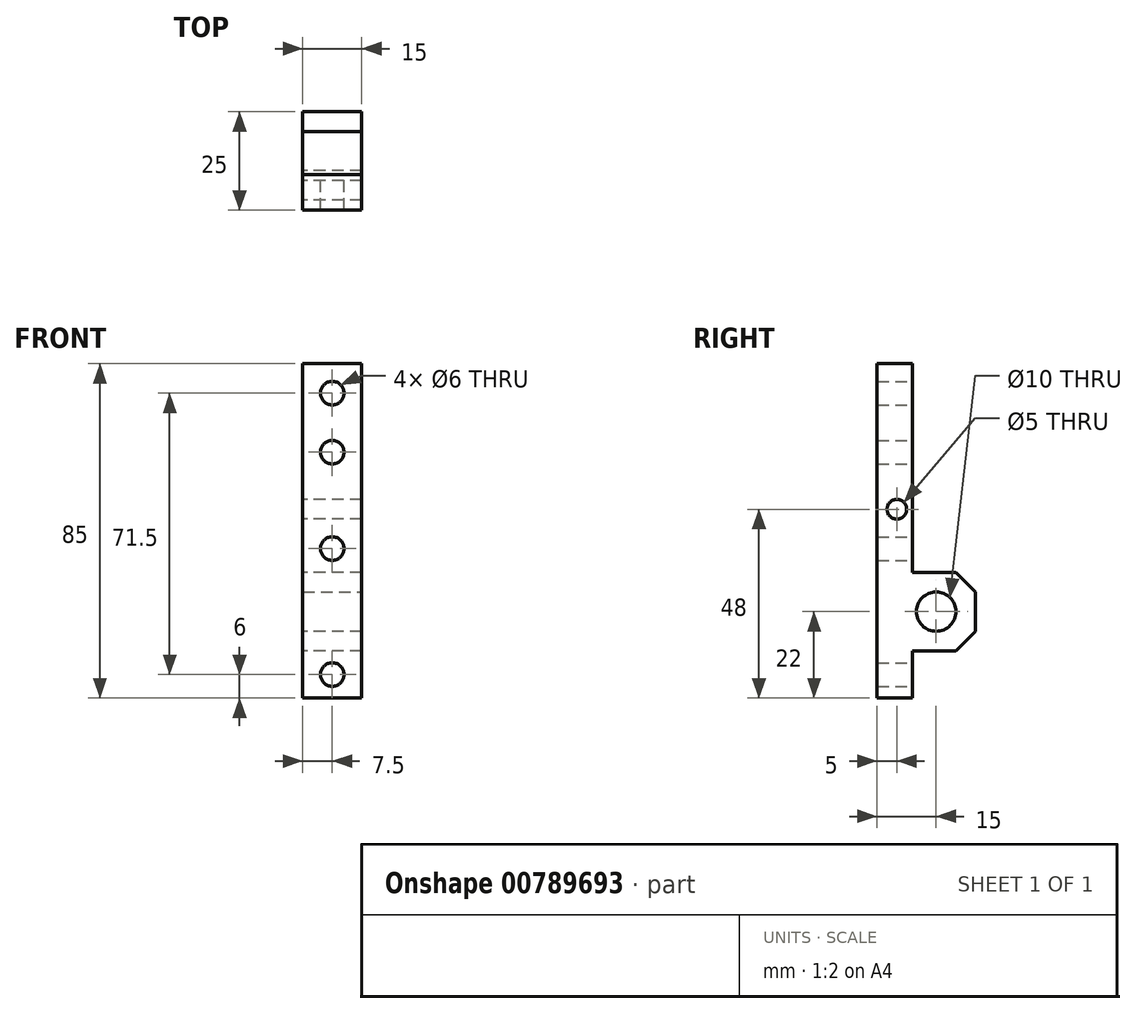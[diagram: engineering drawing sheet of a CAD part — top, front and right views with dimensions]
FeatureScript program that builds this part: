
annotation { "Feature Type Name" : "Feature", "Feature Type Description" : "" }
export const myFeature = defineFeature(function(context is Context, id is Id, definition is map)
    precondition{}
    {
        {
            var Q0;
            Q0=qCreatedBy(makeId("Right.planeOp"),FACE);
            var sketch = newSketch(context, id + "F0", { "sketchPlane" : qUnion([Q0])});
            skLineSegment(sketch, "E0", {"start": v(0, 0) * mm, "end": v(0, 85) * mm});
            skLineSegment(sketch, "E1", {"start": v(0, 85) * mm, "end": v(9, 85) * mm});
            skLineSegment(sketch, "E2", {"start": v(9, 85) * mm, "end": v(9, 32) * mm});
            skLineSegment(sketch, "E3", {"start": v(9, 32) * mm, "end": v(25, 32) * mm});
            skLineSegment(sketch, "E4", {"start": v(25, 32) * mm, "end": v(25, 12) * mm});
            skLineSegment(sketch, "E5", {"start": v(25, 12) * mm, "end": v(9, 12) * mm});
            skLineSegment(sketch, "E6", {"start": v(9, 12) * mm, "end": v(9, 0) * mm});
            skLineSegment(sketch, "E7", {"start": v(9, 0) * mm, "end": v(0, 0) * mm});
            skCircle(sketch, "E8", {"center": v(15, 22) * mm, "radius": 5 * mm});
            skCircle(sketch, "E9", {"center": v(5, 48) * mm, "radius": 2.5 * mm});
            skSolve(sketch);
        }
        {
            var Q0;
            Q0 = qSketchRegion(id + "F0", true);
            extrude(context, id + "F1", {"entities" : qUnion([Q0]), "depth" : 15 * mm, "offsetDistance" : 25 * mm});
        }
        {
            var Q0;
            Q0=makeQuery(id+"F1.opExtrude","SWEPT_EDGE",EDGE,{"disambiguationData":[OSD([sQuery(id+"F0.wireOp",EDGE,"E3"),sQuery(id+"F0.wireOp",EDGE,"E4")])]});
            var Q1;
            Q1=makeQuery(id+"F1.opExtrude","SWEPT_EDGE",EDGE,{"disambiguationData":[OSD([sQuery(id+"F0.wireOp",EDGE,"E4"),sQuery(id+"F0.wireOp",EDGE,"E5")])]});
            chamfer(context, id + "F2", {"entities" : qUnion([Q0, Q1]), "width" : 5 * mm, "tangentPropagation" : true});
        }
        {
            var Q0;
            Q0=makeQuery(id+"F1.opExtrude","SWEPT_FACE",FACE,{"disambiguationData":[OSD([sQuery(id+"F0.wireOp",EDGE,"E2")])]});
            var sketch = newSketch(context, id + "F3", { "sketchPlane" : qUnion([Q0])});
            skCircle(sketch, "E10", {"center": v(-7.5, 77.5) * mm, "radius": 3 * mm});
            skCircle(sketch, "E11", {"center": v(-7.5, 62.5) * mm, "radius": 3 * mm});
            skCircle(sketch, "E12", {"center": v(-7.5, 6) * mm, "radius": 3 * mm});
            skCircle(sketch, "E13", {"center": v(-7.5, 38) * mm, "radius": 3 * mm});
            skSolve(sketch);
        }
        {
            var Q0;
            Q0 = qSketchRegion(id + "F3", true);
            extrude(context, id + "F4", {"entities" : qUnion([Q0]), "operationType" : NewBodyOperationType.REMOVE, "endBound" : BoundingType.UP_TO_NEXT, "oppositeDirection" : true, "depth" : 25 * mm, "offsetDistance" : 25 * mm});
        }
    });
